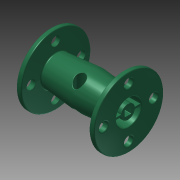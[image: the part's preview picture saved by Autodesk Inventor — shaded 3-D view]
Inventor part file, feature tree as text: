
AUTODESK INVENTOR PART (.ipt)
format: ipt  version: 2015 SP1 (Build 190203100, 203)  size: 1,040,384 bytes
history: native  units: in
note: dims shown in document units (in); Inventor stores cm internally (conversion verified against a paired STEP export)
features: mirror x1, other x1, imported_body x1
ambient origin geometry x8: Origin, YZ Plane, XZ Plane, XY Plane, X Axis, Y Axis, Z Axis, Center Point
bodies: Body1 (feature_tree)
feature tree (3):
  mirror  "Mirror1"
  other  "276-1546-002 Rev31"
  imported_body  "Base1"
